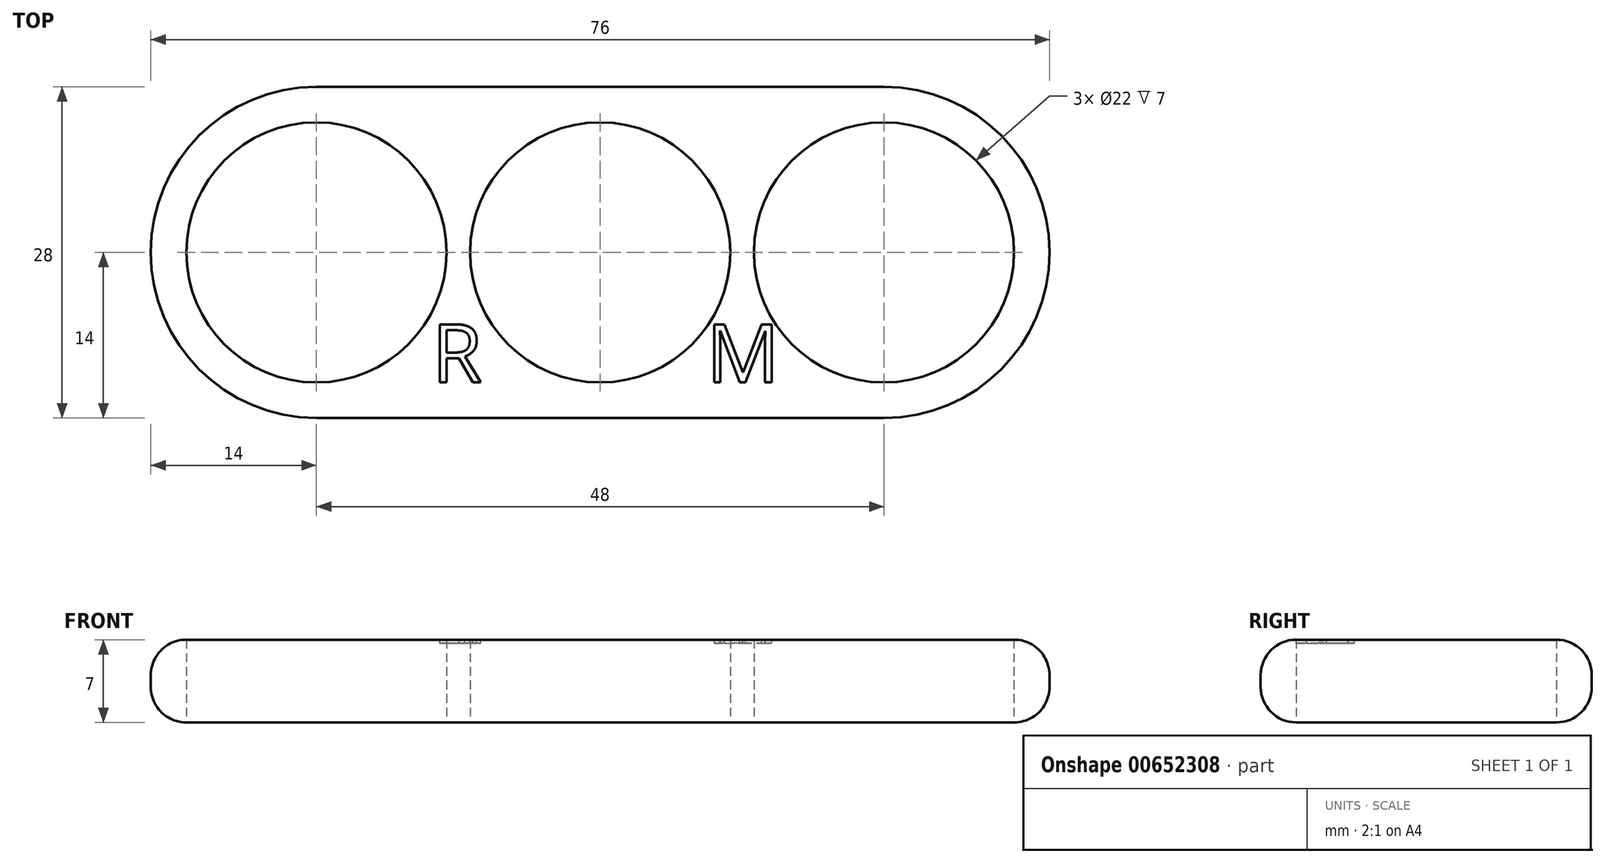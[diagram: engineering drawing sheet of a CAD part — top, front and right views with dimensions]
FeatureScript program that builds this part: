
annotation { "Feature Type Name" : "Feature", "Feature Type Description" : "" }
export const myFeature = defineFeature(function(context is Context, id is Id, definition is map)
    precondition{}
    {
        {
            var Q0;
            Q0=qCreatedBy(makeId("Top.planeOp"),FACE);
            var sketch = newSketch(context, id + "F0", { "sketchPlane" : qUnion([Q0])});
            skArc(sketch, "E0", {"start": v(0, 11) * mm, "mid": v(-11, 0) * mm, "end": v(0, -11) * mm});
            skLineSegment(sketch, "E1", {"start": v(0, 56.07) * mm, "end": v(0, 11) * mm, "construction": true});
            skLineSegment(sketch, "E2", {"start": v(-38, 56.32) * mm, "end": v(-38, -55.95) * mm, "construction": true});
            skArc(sketch, "E3", {"start": v(-24, 14) * mm, "mid": v(-38, 0) * mm, "end": v(-24, -14) * mm});
            skLineSegment(sketch, "E4", {"start": v(0, 14) * mm, "end": v(-24, 14) * mm});
            skLineSegment(sketch, "E5", {"start": v(0, -14) * mm, "end": v(-24, -14) * mm});
            skLineSegment(sketch, "E6", {"start": v(0, 14) * mm, "end": v(0, 11) * mm});
            skLineSegment(sketch, "E7.trimOffspring", {"start": v(0, -11) * mm, "end": v(0, -55.82) * mm, "construction": true});
            skLineSegment(sketch, "E8.trimOffspring", {"start": v(0, -11) * mm, "end": v(0, -14) * mm});
            skCircle(sketch, "E9", {"center": v(-24, 0) * mm, "radius": 11 * mm});
            skSolve(sketch);
        }
        {
            var Q0;
            Q0 = qSketchRegion(id + "F0", true);
            extrude(context, id + "F1", {"entities" : qUnion([Q0]), "depth" : 7 * mm, "offsetDistance" : 25 * mm});
        }
        {
            var Q0;
            Q0=makeQuery(id+"F1.opExtrude","SWEPT_BODY",BODY,{"disambiguationData":[OSD([sQuery(id+"F0.wireOp",EDGE,"E0"),sQuery(id+"F0.wireOp",EDGE,"E3"),sQuery(id+"F0.wireOp",EDGE,"E4"),sQuery(id+"F0.wireOp",EDGE,"E5"),sQuery(id+"F0.wireOp",EDGE,"E6"),sQuery(id+"F0.wireOp",EDGE,"E8.trimOffspring")])]});
            var Q1;
            Q1=qCreatedBy(makeId("Right.planeOp"),FACE);
            mirror(context, id + "F2", {"operationType" : NewBodyOperationType.ADD, "entities" : qUnion([Q0]), "mirrorPlane" : qUnion([Q1])});
        }
        {
            var Q0;
            Q0=makeQuery(id+"F2.opPattern","COPY",EDGE,{"derivedFrom":makeQuery(id+"F1.opExtrude","CAP_EDGE",EDGE,{"disambiguationData":[OSD([sQuery(id+"F0.wireOp",EDGE,"E3")])],"isStart":true}),"instanceName":"1"});
            fillet(context, id + "F3", {"entities" : qUnion([Q0]), "radius" : 3 * mm, "tangentPropagation" : true, "allowEdgeOverflow" : false});
        }
        {
            var Q0;
            Q0=makeQuery(id+"F2.opPattern","COPY",EDGE,{"derivedFrom":makeQuery(id+"F1.opExtrude","CAP_EDGE",EDGE,{"disambiguationData":[OSD([sQuery(id+"F0.wireOp",EDGE,"E3")])],"isStart":false}),"instanceName":"1"});
            var Q1;
            {var subQ0=sQuery(id+"F0.wireOp",EDGE,"E4");var subQ1=sQuery(id+"F0.wireOp",EDGE,"E3");Q1=makeQuery(id+"F2.opPattern","COPY",EDGE,{"derivedFrom":makeQuery(id+"FR4a9zPW414S7ui_1.opFillet","BLEND_EDGE",EDGE,{"blendedFrom":[makeQuery(id+"F1.opExtrude","SWEPT_EDGE",EDGE,{"disambiguationData":[OSD([subQ1,subQ0])]}),makeQuery(id+"F1.opExtrude","CAP_FACE",FACE,{"disambiguationData":[OSD([sQuery(id+"F0.wireOp",EDGE,"E0"),subQ1,subQ0,sQuery(id+"F0.wireOp",EDGE,"E5"),sQuery(id+"F0.wireOp",EDGE,"E6"),sQuery(id+"F0.wireOp",EDGE,"E8.trimOffspring")])],"isStart":false})],"blendedInto":[makeQuery(id+"F1.opExtrude","CAP_FACE",FACE,{"disambiguationData":[OSD([sQuery(id+"F0.wireOp",EDGE,"E0"),subQ1,subQ0,sQuery(id+"F0.wireOp",EDGE,"E5"),sQuery(id+"F0.wireOp",EDGE,"E6"),sQuery(id+"F0.wireOp",EDGE,"E8.trimOffspring")])],"isStart":false})]}),"instanceName":"1"});}
            var Q2;
            {var subQ0=makeQuery(id+"F1.opExtrude","CAP_EDGE",EDGE,{"disambiguationData":[OSD([sQuery(id+"F0.wireOp",EDGE,"E4")])],"isStart":false});Q2=makeQuery(id+"F2.boolean.opBoolean","MERGE",EDGE,{"derivedFrom":[subQ0,makeQuery(id+"F2.opPattern","COPY",EDGE,{"derivedFrom":subQ0,"instanceName":"1"})]});}
            var Q3;
            {var subQ0=sQuery(id+"F0.wireOp",EDGE,"E4");var subQ1=sQuery(id+"F0.wireOp",EDGE,"E3");Q3=makeQuery(id+"FR4a9zPW414S7ui_1.opFillet","BLEND_EDGE",EDGE,{"blendedFrom":[makeQuery(id+"F1.opExtrude","SWEPT_EDGE",EDGE,{"disambiguationData":[OSD([subQ1,subQ0])]}),makeQuery(id+"F1.opExtrude","CAP_FACE",FACE,{"disambiguationData":[OSD([sQuery(id+"F0.wireOp",EDGE,"E0"),subQ1,subQ0,sQuery(id+"F0.wireOp",EDGE,"E5"),sQuery(id+"F0.wireOp",EDGE,"E6"),sQuery(id+"F0.wireOp",EDGE,"E8.trimOffspring")])],"isStart":false})],"blendedInto":[makeQuery(id+"F1.opExtrude","CAP_FACE",FACE,{"disambiguationData":[OSD([sQuery(id+"F0.wireOp",EDGE,"E0"),subQ1,subQ0,sQuery(id+"F0.wireOp",EDGE,"E5"),sQuery(id+"F0.wireOp",EDGE,"E6"),sQuery(id+"F0.wireOp",EDGE,"E8.trimOffspring")])],"isStart":false})]});}
            var Q4;
            Q4=makeQuery(id+"F1.opExtrude","CAP_EDGE",EDGE,{"disambiguationData":[OSD([sQuery(id+"F0.wireOp",EDGE,"E3")])],"isStart":false});
            var Q5;
            {var subQ0=sQuery(id+"F0.wireOp",EDGE,"E5");var subQ1=sQuery(id+"F0.wireOp",EDGE,"E3");Q5=makeQuery(id+"FR4a9zPW414S7ui_1.opFillet","BLEND_EDGE",EDGE,{"blendedFrom":[makeQuery(id+"F1.opExtrude","SWEPT_EDGE",EDGE,{"disambiguationData":[OSD([subQ1,subQ0])]}),makeQuery(id+"F1.opExtrude","CAP_FACE",FACE,{"disambiguationData":[OSD([sQuery(id+"F0.wireOp",EDGE,"E0"),subQ1,sQuery(id+"F0.wireOp",EDGE,"E4"),subQ0,sQuery(id+"F0.wireOp",EDGE,"E6"),sQuery(id+"F0.wireOp",EDGE,"E8.trimOffspring")])],"isStart":false})],"blendedInto":[makeQuery(id+"F1.opExtrude","CAP_FACE",FACE,{"disambiguationData":[OSD([sQuery(id+"F0.wireOp",EDGE,"E0"),subQ1,sQuery(id+"F0.wireOp",EDGE,"E4"),subQ0,sQuery(id+"F0.wireOp",EDGE,"E6"),sQuery(id+"F0.wireOp",EDGE,"E8.trimOffspring")])],"isStart":false})]});}
            var Q6;
            {var subQ0=makeQuery(id+"F1.opExtrude","CAP_EDGE",EDGE,{"disambiguationData":[OSD([sQuery(id+"F0.wireOp",EDGE,"E5")])],"isStart":false});Q6=makeQuery(id+"F2.boolean.opBoolean","MERGE",EDGE,{"derivedFrom":[subQ0,makeQuery(id+"F2.opPattern","COPY",EDGE,{"derivedFrom":subQ0,"instanceName":"1"})]});}
            var Q7;
            {var subQ0=sQuery(id+"F0.wireOp",EDGE,"E5");var subQ1=sQuery(id+"F0.wireOp",EDGE,"E3");Q7=makeQuery(id+"F2.opPattern","COPY",EDGE,{"derivedFrom":makeQuery(id+"FR4a9zPW414S7ui_1.opFillet","BLEND_EDGE",EDGE,{"blendedFrom":[makeQuery(id+"F1.opExtrude","SWEPT_EDGE",EDGE,{"disambiguationData":[OSD([subQ1,subQ0])]}),makeQuery(id+"F1.opExtrude","CAP_FACE",FACE,{"disambiguationData":[OSD([sQuery(id+"F0.wireOp",EDGE,"E0"),subQ1,sQuery(id+"F0.wireOp",EDGE,"E4"),subQ0,sQuery(id+"F0.wireOp",EDGE,"E6"),sQuery(id+"F0.wireOp",EDGE,"E8.trimOffspring")])],"isStart":false})],"blendedInto":[makeQuery(id+"F1.opExtrude","CAP_FACE",FACE,{"disambiguationData":[OSD([sQuery(id+"F0.wireOp",EDGE,"E0"),subQ1,sQuery(id+"F0.wireOp",EDGE,"E4"),subQ0,sQuery(id+"F0.wireOp",EDGE,"E6"),sQuery(id+"F0.wireOp",EDGE,"E8.trimOffspring")])],"isStart":false})]}),"instanceName":"1"});}
            fillet(context, id + "F4", {"entities" : qUnion([Q0, Q1, Q2, Q3, Q4, Q5, Q6, Q7]), "radius" : 3 * mm, "tangentPropagation" : true, "allowEdgeOverflow" : false});
        }
        {
            var Q0;
            {var subQ0=makeQuery(id+"F1.opExtrude","CAP_FACE",FACE,{"disambiguationData":[OSD([sQuery(id+"F0.wireOp",EDGE,"E0"),sQuery(id+"F0.wireOp",EDGE,"E3"),sQuery(id+"F0.wireOp",EDGE,"E4"),sQuery(id+"F0.wireOp",EDGE,"E5"),sQuery(id+"F0.wireOp",EDGE,"E6"),sQuery(id+"F0.wireOp",EDGE,"E8.trimOffspring"),sQuery(id+"F0.wireOp",EDGE,"E9")])],"isStart":false});Q0=makeQuery(id+"F4.opFillet","SPLIT",FACE,{"disambiguationData":[OD(1.0)],"derivedFrom":makeQuery(id+"F2.boolean.opBoolean","MERGE",FACE,{"derivedFrom":[subQ0,makeQuery(id+"F2.opPattern","COPY",FACE,{"derivedFrom":subQ0,"instanceName":"1"})]})});}
            var sketch = newSketch(context, id + "F5", { "sketchPlane" : qUnion([Q0])});
            skText(sketch, "E10", { "text": "R", "fontName": "OpenSans-Regular.ttf"});
            skLineSegment(sketch, "E11", {"start": v(-9.64, -6.04) * mm, "end": v(14.08, -6.04) * mm, "construction": true});
            skLineSegment(sketch, "E12", {"start": v(-9.64, -11) * mm, "end": v(14.43, -11) * mm, "construction": true});
            skText(sketch, "E13", { "text": "M", "fontName": "OpenSans-Regular.ttf"});
            const initialGuessF5  = {"E10": [-0.01423, -0.011, 1, 0, 0.00496], "E13": [0.00896, -0.011, 1, 0, 0.00496]};
            skSetInitialGuess(sketch, initialGuessF5);
            skSolve(sketch);
        }
        {
            var Q0;
            Q0 = qSketchRegion(id + "F5", true);
            extrude(context, id + "F6", {"entities" : qUnion([Q0]), "operationType" : NewBodyOperationType.REMOVE, "oppositeDirection" : true, "depth" : .3 * mm, "offsetDistance" : 25 * mm});
        }
    });
